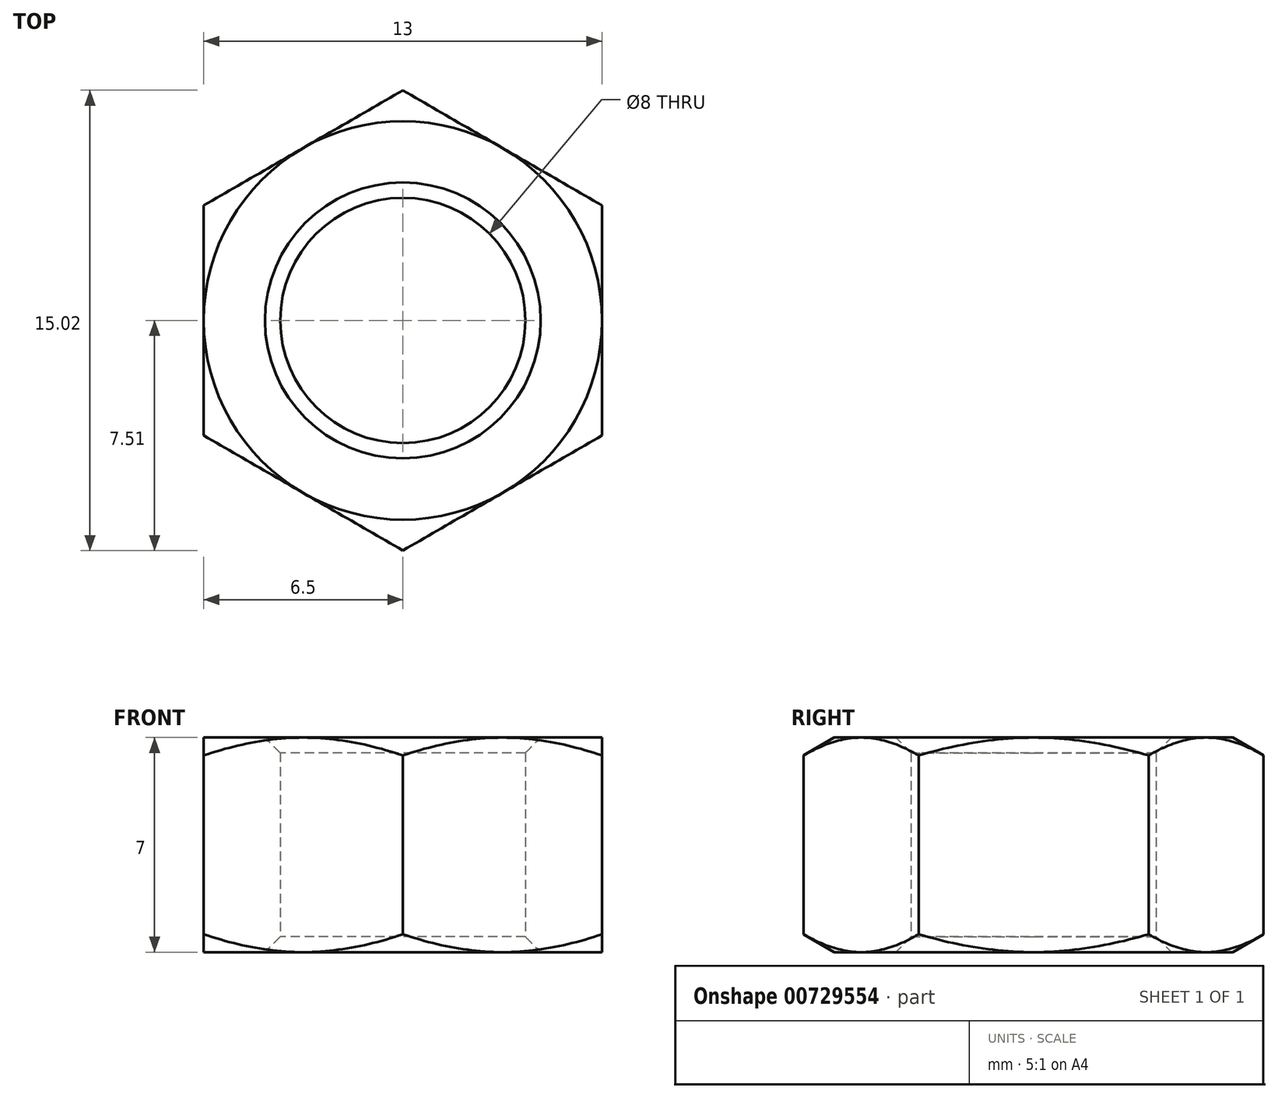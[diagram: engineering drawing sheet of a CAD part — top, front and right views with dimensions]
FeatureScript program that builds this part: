
annotation { "Feature Type Name" : "Feature", "Feature Type Description" : "" }
export const myFeature = defineFeature(function(context is Context, id is Id, definition is map)
    precondition{}
    {
        {
            var Q0;
            Q0=qCreatedBy(makeId("Top.planeOp"),FACE);
            var sketch = newSketch(context, id + "F0", { "sketchPlane" : qUnion([Q0])});
            skCircle(sketch, "E0.cCircle", {"center": v(0, 0) * mm, "radius": 6.5 * mm, "construction": true});
            skLineSegment(sketch, "E0.0", {"start": v(6.5, -3.75) * mm, "end": v(0, -7.5) * mm});
            skLineSegment(sketch, "E0.1", {"start": v(0, -7.5) * mm, "end": v(-6.5, -3.75) * mm});
            skLineSegment(sketch, "E0.2", {"start": v(-6.5, -3.75) * mm, "end": v(-6.5, 3.75) * mm});
            skLineSegment(sketch, "E0.3", {"start": v(-6.5, 3.75) * mm, "end": v(0, 7.5) * mm});
            skLineSegment(sketch, "E0.4", {"start": v(0, 7.5) * mm, "end": v(6.5, 3.75) * mm});
            skLineSegment(sketch, "E0.5", {"start": v(6.5, 3.75) * mm, "end": v(6.5, -3.75) * mm});
            skPoint(sketch, "E0.0.midPoint", {"position": v(3.25, -5.63) * mm});
            skCircle(sketch, "E1", {"center": v(0, 0) * mm, "radius": 4 * mm});
            skSolve(sketch);
        }
        {
            var Q0;
            Q0 = qSketchRegion(id + "F0", true);
            var Q1;
            Q1=makeQuery(id+"F0.imprint","IMPRINT",FACE,{"disambiguationData":[TD([[makeQuery(id+"F0.imprint","IMPRINT",EDGE,{"derivedFrom":sQuery(id+"F0.wireOp",EDGE,"E0.0")}),-1.0]])]});
            extrude(context, id + "F1", {"entities" : qUnion([Q0, Q1]), "depth" : 7 * mm, "offsetDistance" : 25 * mm});
        }
        {
            var Q0;
            Q0=qCreatedBy(makeId("Front.planeOp"),FACE);
            var sketch = newSketch(context, id + "F2", { "sketchPlane" : qUnion([Q0])});
            skLineSegment(sketch, "E2", {"start": v(0, 7) * mm, "end": v(0, 0) * mm, "construction": true});
            skLineSegment(sketch, "E3", {"start": v(0, 0) * mm, "end": v(0, 7) * mm, "construction": true});
            skLineSegment(sketch, "E4", {"start": v(0, 7) * mm, "end": v(0, 3.5) * mm, "construction": true});
            skLineSegment(sketch, "E5", {"start": v(0, 3.5) * mm, "end": v(0, 0) * mm, "construction": true});
            skLineSegment(sketch, "E6", {"start": v(0, 3.5) * mm, "end": v(6.5, 3.5) * mm, "construction": true});
            skLineSegment(sketch, "E7", {"start": v(6.5, 7) * mm, "end": v(12.2, 7) * mm});
            skLineSegment(sketch, "E8", {"start": v(12.2, 7) * mm, "end": v(12.2, 3.7) * mm});
            skLineSegment(sketch, "E9", {"start": v(12.2, 3.7) * mm, "end": v(6.5, 7) * mm});
            skLineSegment(sketch, "E10.MirrorCS", {"start": v(6.5, 0) * mm, "end": v(12.2, 0) * mm});
            skLineSegment(sketch, "E11.MirrorCS", {"start": v(12.2, 3.3) * mm, "end": v(6.5, 0) * mm});
            skLineSegment(sketch, "E12.MirrorCS", {"start": v(12.2, 0) * mm, "end": v(12.2, 3.3) * mm});
            skSolve(sketch);
        }
        {
            var Q0;
            Q0 = qSketchRegion(id + "F2", true);
            var Q1;
            Q1=sQuery(id+"F2.wireOp",EDGE,"E5");
            revolve(context, id + "F3", {"operationType" : NewBodyOperationType.REMOVE, "surfaceOperationType" : NewSurfaceOperationType.NEW, "entities" : qUnion([Q0]), "axis" : qUnion([Q1]), "revolveType" : RevolveType.FULL, "oppositeDirection" : true});
        }
        {
            var Q0;
            Q0=makeQuery(id+"F1.opExtrude","SWEPT_FACE",FACE,{"disambiguationData":[OSD([sQuery(id+"F0.wireOp",EDGE,"E1")])]});
            chamfer(context, id + "F4", {"entities" : qUnion([Q0]), "width" : 0.5 * mm, "tangentPropagation" : true});
        }
    });
